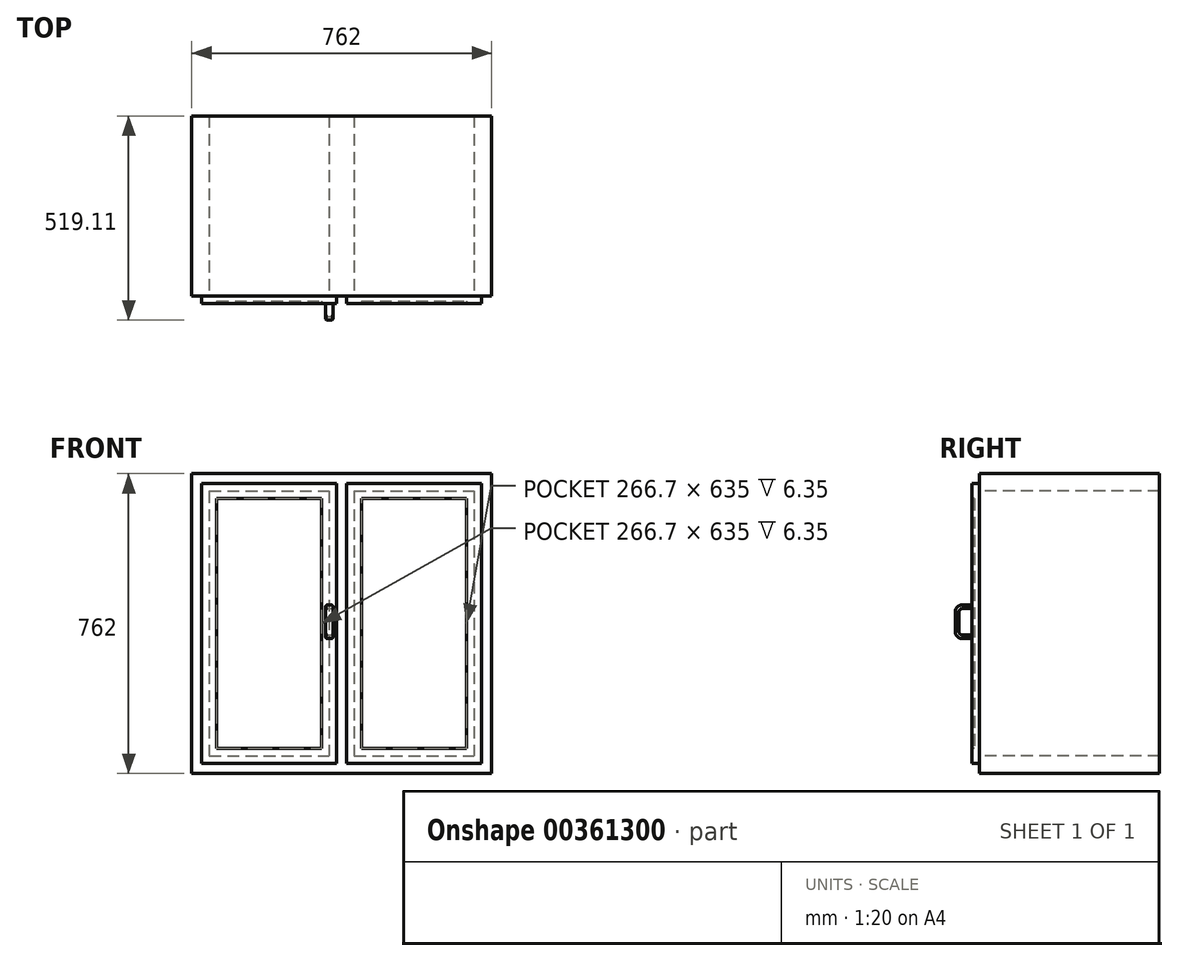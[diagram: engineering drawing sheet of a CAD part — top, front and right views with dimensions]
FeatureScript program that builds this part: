
annotation { "Feature Type Name" : "Feature", "Feature Type Description" : "" }
export const myFeature = defineFeature(function(context is Context, id is Id, definition is map)
    precondition{}
    {
        {
            var Q0;
            Q0=qCreatedBy(makeId("Top.planeOp"),FACE);
            var sketch = newSketch(context, id + "F0", { "sketchPlane" : qUnion([Q0])});
            skLineSegment(sketch, "E0.bottom", {"start": v(-381, 228.6) * mm, "end": v(381, 228.6) * mm});
            skLineSegment(sketch, "E0.top", {"start": v(-381, -228.6) * mm, "end": v(381, -228.6) * mm});
            skLineSegment(sketch, "E0.left", {"start": v(-381, 228.6) * mm, "end": v(-381, -228.6) * mm});
            skLineSegment(sketch, "E0.right", {"start": v(381, 228.6) * mm, "end": v(381, -228.6) * mm});
            skPoint(sketch, "E0.middle", {"position": v(0, 0) * mm});
            skSolve(sketch);
        }
        {
            var Q0;
            Q0=qSketchRegion(id+"F0",true);
            extrude(context, id + "F1", {"entities" : qUnion([Q0]), "depth" : 381 * mm, "hasSecondDirection" : true, "secondDirectionOppositeDirection" : true, "secondDirectionDepth" : 381 * mm});
        }
        {
            var Q0;
            Q0=makeQuery(id+"F1.opExtrude","SWEPT_FACE",FACE,{"disambiguationData":[OSD([sQuery(id+"F0.wireOp",EDGE,"E0.top")])]});
            var sketch = newSketch(context, id + "F2", { "sketchPlane" : qUnion([Q0])});
            skLineSegment(sketch, "E1.bottom", {"start": v(-336.55, 336.55) * mm, "end": v(-31.75, 336.55) * mm});
            skLineSegment(sketch, "E1.top", {"start": v(-336.55, -336.55) * mm, "end": v(-31.75, -336.55) * mm});
            skLineSegment(sketch, "E1.left", {"start": v(-336.55, 336.55) * mm, "end": v(-336.55, -336.55) * mm});
            skLineSegment(sketch, "E1.right", {"start": v(-31.75, 336.55) * mm, "end": v(-31.75, -336.55) * mm});
            skPoint(sketch, "E1.middle", {"position": v(-184.15, 0) * mm});
            skLineSegment(sketch, "E2.bottom", {"start": v(31.75, 336.55) * mm, "end": v(336.55, 336.55) * mm});
            skLineSegment(sketch, "E2.top", {"start": v(31.75, -336.55) * mm, "end": v(336.55, -336.55) * mm});
            skLineSegment(sketch, "E2.left", {"start": v(31.75, 336.55) * mm, "end": v(31.75, -336.55) * mm});
            skLineSegment(sketch, "E2.right", {"start": v(336.55, 336.55) * mm, "end": v(336.55, -336.55) * mm});
            skPoint(sketch, "E2.middle", {"position": v(184.15, 0) * mm});
            skSolve(sketch);
        }
        {
            var Q0;
            Q0=qSketchRegion(id+"F2",true);
            extrude(context, id + "F3", {"entities" : qUnion([Q0]), "operationType" : NewBodyOperationType.REMOVE, "endBound" : BoundingType.UP_TO_NEXT, "oppositeDirection" : true, "depth" : 25.4 * mm});
        }
        {
            var Q0;
            Q0=makeQuery(id+"F1.opExtrude","SWEPT_FACE",FACE,{"disambiguationData":[OSD([sQuery(id+"F0.wireOp",EDGE,"E0.top")])]});
            var sketch = newSketch(context, id + "F4", { "sketchPlane" : qUnion([Q0])});
            skLineSegment(sketch, "E3.bottom", {"start": v(-355.6, 355.6) * mm, "end": v(-12.7, 355.6) * mm});
            skLineSegment(sketch, "E3.top", {"start": v(-355.6, -355.6) * mm, "end": v(-12.7, -355.6) * mm});
            skLineSegment(sketch, "E3.left", {"start": v(-355.6, 355.6) * mm, "end": v(-355.6, -355.6) * mm});
            skLineSegment(sketch, "E3.right", {"start": v(-12.7, 355.6) * mm, "end": v(-12.7, -355.6) * mm});
            skPoint(sketch, "E3.middle", {"position": v(-184.15, 0) * mm});
            skLineSegment(sketch, "E4.bottom", {"start": v(12.7, 355.6) * mm, "end": v(355.6, 355.6) * mm});
            skLineSegment(sketch, "E4.top", {"start": v(12.7, -355.6) * mm, "end": v(355.6, -355.6) * mm});
            skLineSegment(sketch, "E4.left", {"start": v(12.7, 355.6) * mm, "end": v(12.7, -355.6) * mm});
            skLineSegment(sketch, "E4.right", {"start": v(355.6, 355.6) * mm, "end": v(355.6, -355.6) * mm});
            skPoint(sketch, "E4.middle", {"position": v(184.15, 0) * mm});
            skSolve(sketch);
        }
        {
            var Q0;
            Q0=qSketchRegion(id+"F4",true);
            extrude(context, id + "F5", {"entities" : qUnion([Q0]), "operationType" : NewBodyOperationType.ADD, "depth" : 19.05 * mm});
        }
        {
            var Q0;
            Q0=makeQuery(id+"F5.opExtrude","CAP_FACE",FACE,{"disambiguationData":[OSD([sQuery(id+"F4.wireOp",EDGE,"E3.bottom"),sQuery(id+"F4.wireOp",EDGE,"E3.top"),sQuery(id+"F4.wireOp",EDGE,"E3.left"),sQuery(id+"F4.wireOp",EDGE,"E3.right")])],"isStart":false});
            var sketch = newSketch(context, id + "F6", { "sketchPlane" : qUnion([Q0])});
            skLineSegment(sketch, "E5.bottom", {"start": v(-317.5, 317.5) * mm, "end": v(-50.8, 317.5) * mm});
            skLineSegment(sketch, "E5.top", {"start": v(-317.5, -317.5) * mm, "end": v(-50.8, -317.5) * mm});
            skLineSegment(sketch, "E5.left", {"start": v(-317.5, 317.5) * mm, "end": v(-317.5, -317.5) * mm});
            skLineSegment(sketch, "E5.right", {"start": v(-50.8, 317.5) * mm, "end": v(-50.8, -317.5) * mm});
            skPoint(sketch, "E5.middle", {"position": v(-184.15, 0) * mm});
            skLineSegment(sketch, "E6.bottom", {"start": v(50.8, 317.5) * mm, "end": v(317.5, 317.5) * mm});
            skLineSegment(sketch, "E6.top", {"start": v(50.8, -317.5) * mm, "end": v(317.5, -317.5) * mm});
            skLineSegment(sketch, "E6.left", {"start": v(50.8, 317.5) * mm, "end": v(50.8, -317.5) * mm});
            skLineSegment(sketch, "E6.right", {"start": v(317.5, 317.5) * mm, "end": v(317.5, -317.5) * mm});
            skPoint(sketch, "E6.middle", {"position": v(184.15, 0) * mm});
            skSolve(sketch);
        }
        {
            var Q0;
            Q0=qSketchRegion(id+"F6",true);
            extrude(context, id + "F7", {"entities" : qUnion([Q0]), "operationType" : NewBodyOperationType.REMOVE, "oppositeDirection" : true, "depth" : 6.35 * mm});
        }
        {
            var Q0;
            Q0=makeQuery(id+"F5.opExtrude","CAP_FACE",FACE,{"disambiguationData":[OSD([sQuery(id+"F4.wireOp",EDGE,"E3.bottom"),sQuery(id+"F4.wireOp",EDGE,"E3.top"),sQuery(id+"F4.wireOp",EDGE,"E3.left"),sQuery(id+"F4.wireOp",EDGE,"E3.right")])],"isStart":false});
            var sketch = newSketch(context, id + "F8", { "sketchPlane" : qUnion([Q0])});
            skArc(sketch, "E7", {"start": v(-36.51, 47.63) * mm, "mid": v(-41.28, 42.86) * mm, "end": v(-36.51, 38.1) * mm});
            skLineSegment(sketch, "E8", {"start": v(-36.51, 47.63) * mm, "end": v(-26.99, 47.63) * mm});
            skLineSegment(sketch, "E9", {"start": v(-36.51, 38.1) * mm, "end": v(-26.99, 38.1) * mm});
            skArc(sketch, "E10", {"start": v(-26.99, 38.1) * mm, "mid": v(-22.23, 42.86) * mm, "end": v(-26.99, 47.63) * mm});
            skLineSegment(sketch, "E11", {"start": v(-12.7, 0) * mm, "end": v(-50.8, 0) * mm, "construction": true});
            skLineSegment(sketch, "E12", {"start": v(-31.75, 0) * mm, "end": v(-31.75, 38.1) * mm, "construction": true});
            skLineSegment(sketch, "E13", {"start": v(-31.75, 38.1) * mm, "end": v(-31.75, 42.86) * mm, "construction": true});
            skLineSegment(sketch, "E14", {"start": v(-31.75, 42.86) * mm, "end": v(-31.75, 47.63) * mm, "construction": true});
            skSolve(sketch);
        }
        {
            var Q0;
            Q0=makeQuery(id+"F1.opExtrude","SWEPT_FACE",FACE,{"disambiguationData":[OSD([sQuery(id+"F0.wireOp",EDGE,"E0.left")])]});
            var Q1;
            Q1=sQuery(id+"F8.wireOp",VERTEX,"E12.end");
            cPlane(context, id + "F9", {"entities" : qUnion([Q0, Q1]), "cplaneType" : CPlaneType.PLANE_POINT, "offset" : 25.4 * mm, "width" : 152.4 * mm, "height" : 152.4 * mm});
        }
        {
            var Q0;
            Q0=qCreatedBy(id+"F9.planeOp",FACE);
            var sketch = newSketch(context, id + "F10", { "sketchPlane" : qUnion([Q0])});
            skLineSegment(sketch, "E15", {"start": v(247.65, 42.86) * mm, "end": v(273.05, 42.86) * mm});
            skLineSegment(sketch, "E16", {"start": v(285.75, 30.16) * mm, "end": v(285.75, -20.64) * mm});
            skLineSegment(sketch, "E17", {"start": v(273.05, -33.34) * mm, "end": v(247.65, -33.34) * mm});
            skPoint(sketch, "E18.visualSharp", {"position": v(285.75, 42.86) * mm});
            skArc(sketch, "E18.filletArc", {"start": v(285.75, 30.16) * mm, "mid": v(282.03, 39.14) * mm, "end": v(273.05, 42.86) * mm});
            skPoint(sketch, "E19.visualSharp", {"position": v(285.75, -33.34) * mm});
            skArc(sketch, "E19.filletArc", {"start": v(273.05, -33.34) * mm, "mid": v(282.03, -29.62) * mm, "end": v(285.75, -20.64) * mm});
            skSolve(sketch);
        }
        {
            var Q0;
            Q0=makeQuery(id+"F8.imprint","IMPRINT",FACE,{"disambiguationData":[TD([[makeQuery(id+"F8.imprint","IMPRINT",EDGE,{"derivedFrom":sQuery(id+"F8.wireOp",EDGE,"E7")}),1.0]])]});
            var Q1;
            Q1=sQuery(id+"F10.wireOp",EDGE,"E15");
            var Q2;
            Q2=sQuery(id+"F10.wireOp",EDGE,"E18.filletArc");
            var Q3;
            Q3=sQuery(id+"F10.wireOp",EDGE,"E16");
            var Q4;
            Q4=sQuery(id+"F10.wireOp",EDGE,"E19.filletArc");
            var Q5;
            Q5=sQuery(id+"F10.wireOp",EDGE,"E17");
            sweep(context, id + "F11", {"operationType" : NewBodyOperationType.ADD, "profiles" : qUnion([Q0]), "path" : qUnion([Q1, Q2, Q3, Q4, Q5])});
        }
    });
